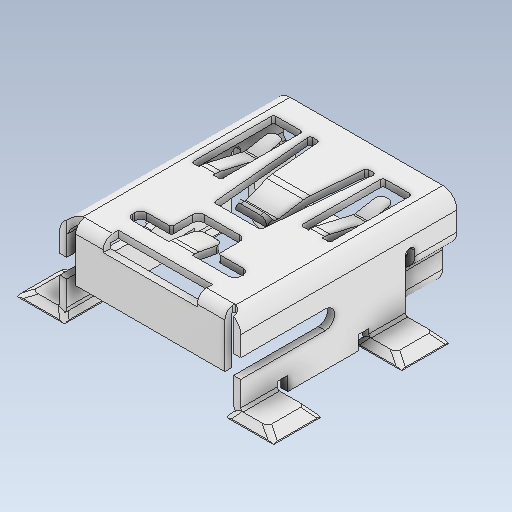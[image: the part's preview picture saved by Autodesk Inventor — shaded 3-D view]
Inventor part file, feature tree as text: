
AUTODESK INVENTOR PART (.ipt)
format: ipt  version: 2020 (Build 240168000, 168)  size: 397,824 bytes
history: native  units: in
note: dims shown in document units (in); Inventor stores cm internally (conversion verified against a paired STEP export)
features: fillet x1
ambient origin geometry x8: Origin, YZ Plane, XZ Plane, XY Plane, X Axis, Y Axis, Z Axis, Center Point
bodies: Solid1 (feature_tree)
feature tree (1):
  fillet  "Fillet14"  [1 undecoded]
note: 1 required parameter value undecoded (feature->parameter linkage not recoverable at this tier; creation-order binding heuristic only, values carry confidence <= 0.55)
